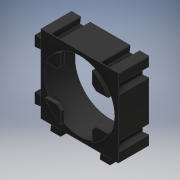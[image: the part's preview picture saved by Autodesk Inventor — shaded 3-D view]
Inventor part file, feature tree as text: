
AUTODESK INVENTOR PART (.ipt)
format: ipt  version: 2018.3 (Build 223285000, 285)  size: 317,440 bytes
history: native  units: mm
features: extrude x5, sketch x5, other x1
ambient origin geometry x8: Origin, YZ Plane, XZ Plane, XY Plane, X Axis, Y Axis, Z Axis, Center Point
bodies: Body1 (feature_tree)
feature tree (11):
  other  "Sólido1"
  extrude  "Extrusión1"  Depth=20.0mm
  extrude  "Extrusión2"  Depth=20.0mm
  extrude  "Extrusión3"  Depth=0.1mm
  extrude  "Extrusión4"  Depth=0.1mm
  extrude  "Extrusión5"  Depth=0.1mm
  sketch  "Boceto1"  dims[d0=18.0mm d1=20.0mm]
  sketch  "Boceto2"  dims[d2=20.0mm d3=2.5mm]
  sketch  "Boceto3"  dims[d4=2.3mm d8=0.1mm]
  sketch  "Boceto4"  dims[d9=0.1mm d10=0.1mm]
  sketch  "Boceto5"  dims[d11=0.1mm d12=0.1mm d13=0.1mm d14=0.1mm d15=0.1mm d16=0.1mm d17=0.1mm d18=0.1mm d19=0.1mm d20=7.8mm d21=0.0mm d22=1.35mm d23=1.35mm d24=1.7mm d25=0.2mm d26=0.0mm d27=0.2mm d28=0.0mm d29=0.2mm d30=0.0mm d31=6.0mm d32=6.0mm d33=1.0mm d34=1.0mm d35=1.0mm d36=1.0mm d37=1.0mm d38=1.0mm d39=1.0mm d40=1.0mm d41=0.8mm d42=0.0mm d43=0.1mm]
